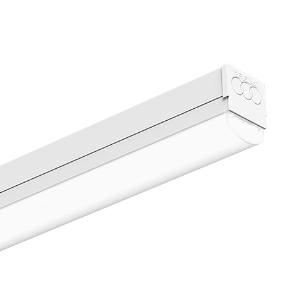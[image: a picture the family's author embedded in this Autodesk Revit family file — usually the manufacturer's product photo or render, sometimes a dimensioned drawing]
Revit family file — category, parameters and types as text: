
# Revit family: 3f_filippi_-_3f_zeta_d_3f_filippi_-_10965_-_3f_zeta_d_2x18_led_dali_l1194
name_source: partatom
category: Lighting Fixtures
units: mm (PartAtom-declared; Revit-internal decimal feet)

## family parameters
Cut with Voids When Loaded = No
Host = Face
Light Source = No
Part Type = Normal
Room Calculation Point = No
Round Connector Dimension = Use Diameter
Shared = No

## types (1)
- 3F Filippi - 3F Zeta D (1 x LED, 4838 lm, 40 W, 4000 K)
    Apparent Load = 40 VA
    Approval mark = CE
    CIE Flux Codes = 42 71 90 91 100
    Color Rendering = 80
    Color Temperature = 4000 K
    Control Gear = Electronic transformer
    Default Elevation = 1800 mm
    Description = ILLUMINOTECHNICAL
Luminous efficiency 100% (DLOR 91%, ULOR 9%).
Initial luminous flux of the luminaire 4838 lm.
Diffused symmetric distribution.
Installation Interdistance Transv.D = 1.31 x hu - Long.D = 1.25 x hu.
Tabular UGR (CIE 117 - 4H-8H; S=0.25H; 70/50/20): RUG 26.1 - 24.4.
Beam angle: 130° - 112°.
Luminous efficacy 121 lm/W.
Lifetime (L93/B10): 30000 h. (tq+25°C)
Lifetime (L90/B10): 50000 h. (tq+25°C)
Lifetime (L85/B10): 80000 h. (tq+25°C)
Lifetime (L80/B10): 100000 h. (tq+25°C)
Sudden decreased luminous flux after 50000 hours: 0% (C0).
Photobiological safety in compliance with IEC/TR 62778: RG0 risk exempt, (IEC 62471).
In compliance with IEC/EN 62722-2-1 - IEC/EN 62717 standards.

SOURCE
2 linear LED modules 18W/840.
Energy efficiency class (UE 2019/2020 - UE 2019/2015): D.
CIE 13.3 Colour rendering index: CRI >80 (R9 <50%).
IES TM-30 Fidelity Index: Rf = 84 Rg = 95.
CCT nominal colour temperature 4000 K.
Colour initial tolerance (MacAdam): SDCM 3.

MECHANICAL
Housing in hot-galvanised steel, painted in white polyester, obtained through rolling process.
Light unit in hot-galvanised steel, painted in white polyester base with fixing springs and retractable safety hooks in stainless steel.
Curved screen in self-extinguishing polycarbonate, UV stabilised, opal, with smooth outer surface.
End caps in white polycarbonate.
Pair of stainless steel sliding brackets with sliding block screws.
Luminaire with limited surface temperature. - D - (EN 60598-2-24)
Dimensions: 1194x62 mm, height 81 mm. Weight 3.6 kg.
IP40 protection degree.
Mechanical strength to impacts IK06 (1 joule).
Glow-wire test resistance 850°C.

ELECTRICAL
Halogen Free DALI-2 DATI (Parts 251, 252, 253), PUSH-DIM, electronic wiring 230V-50/60Hz, power factor 0.95 at full load, THD <25%, constant output current, SELV, class I, 1 driver, 1 DALI addresse.
Power of the luminaire 40 W.
ENEC - CE.
SAFE FLICKER: PstLM=<1 and SVM=<0.4 (IEC TR 61547-1 and IEC TR 63158), to ensure a more comfortable and safe light.
Luminaire compliant with EN 60598-2-22 for power supply from a centralised emergency system CPSS (Central Power Supply System), not incorporated in the luminaire - high risk areas excluded. The default power and flux are 100% in AC and 15% in DC.
Ambient temperature from 0°C to +25°C.
Temperature class T6 max 85°C.
Relative humidity UR: <85%.

INSTALLATION
Ceiling / Suspended / Wall.
All accessories dedicated to this product are available on the Catalog and on our website www.3F-Filippi.com.

APPLICATIONS
Suitable product for food production plants (HACCP), IFS (Food Version 6), BRC (GSFS Food Version 7).
In commercial environments, exhibition areas, shops and stores.

LIGHT MANAGEMENT
Recommended minimum setting: 10%.
The luminaire, equipped with (DALI-2 DATI) driver, can be controlled manually with 3F Easy Dim technology or automatically/manually with wired or wireless DALI/D2D control systems.
The D2D driver guarantees interoperability with other devices with the same certification by making the following information available:
Device Data (Part 251), Energy Report (Part 252), Diagnosis & Maintenance (Part 253).
In electrical systems without a regulation system (manual or automatic) and DALI bus, a suitable jumper must be made on the DA-DA terminals of the appliance.

WARNING
Luminaire designed for disposal/recycling at end-of-life.
Replaceable (LED only) light source by a professional. Replaceable control gear by a professional.
    Height = 81 mm
    Lamp = 1 x LED
    Lamp Light Flux = 4838 lm
    Lamp Power = 40 W
    Lamp count = 1
    Length = 1194 mm
    Lifetime = 50000 h
    Luminous efficacy = 121 lm/W
    Manufacturer = 3F Filippi
    ModVariant = No
    Model = 3F Filippi - 10965 - 3F Zeta D 2x18 LED DALI L1194
    Mounting Place = Ceiling
    Mounting Type = Pendant
    Number of Poles = 1
    OnlyDefault = Yes
    Power Factor = 1
    Product Name = 3F Filippi - 3F Zeta D
    Product group = pendant luminaire
    ProductGroupID = 9
    Protection Class = Protection class I
    Protection Degree = IP 40
    RLX_Detail_Level = 1
    RLX_Emergency_Light_Flux = 0 lm
    RLX_Emergency_Type = 0
    RLX_Emergency_Type_DB = No
    RlxData = <blob elided: 35605 chars, md5=73e69225>
    Socket = socket
    Standby Power = 0 W
    System Light Flux = 4838 lm
    System Power = 40 W
    Type Comments = Product without accessories
    Type Image = 3ffilippi_3f_zeta_d.jpg
    URL = http://relux.com
    VarID = ---
    Voltage = 0 V
    Weight = 0.00 kg
    Width = 62 mm  [stored 0.203412 ft]

note: [stored X ft] marks values corroborated as IEEE doubles in the binary element streams (Revit-internal decimal feet)

## geometry (parser evidence)
native form markers: Blend x4, Sweep x13
no freeform markers — native parametric forms only
